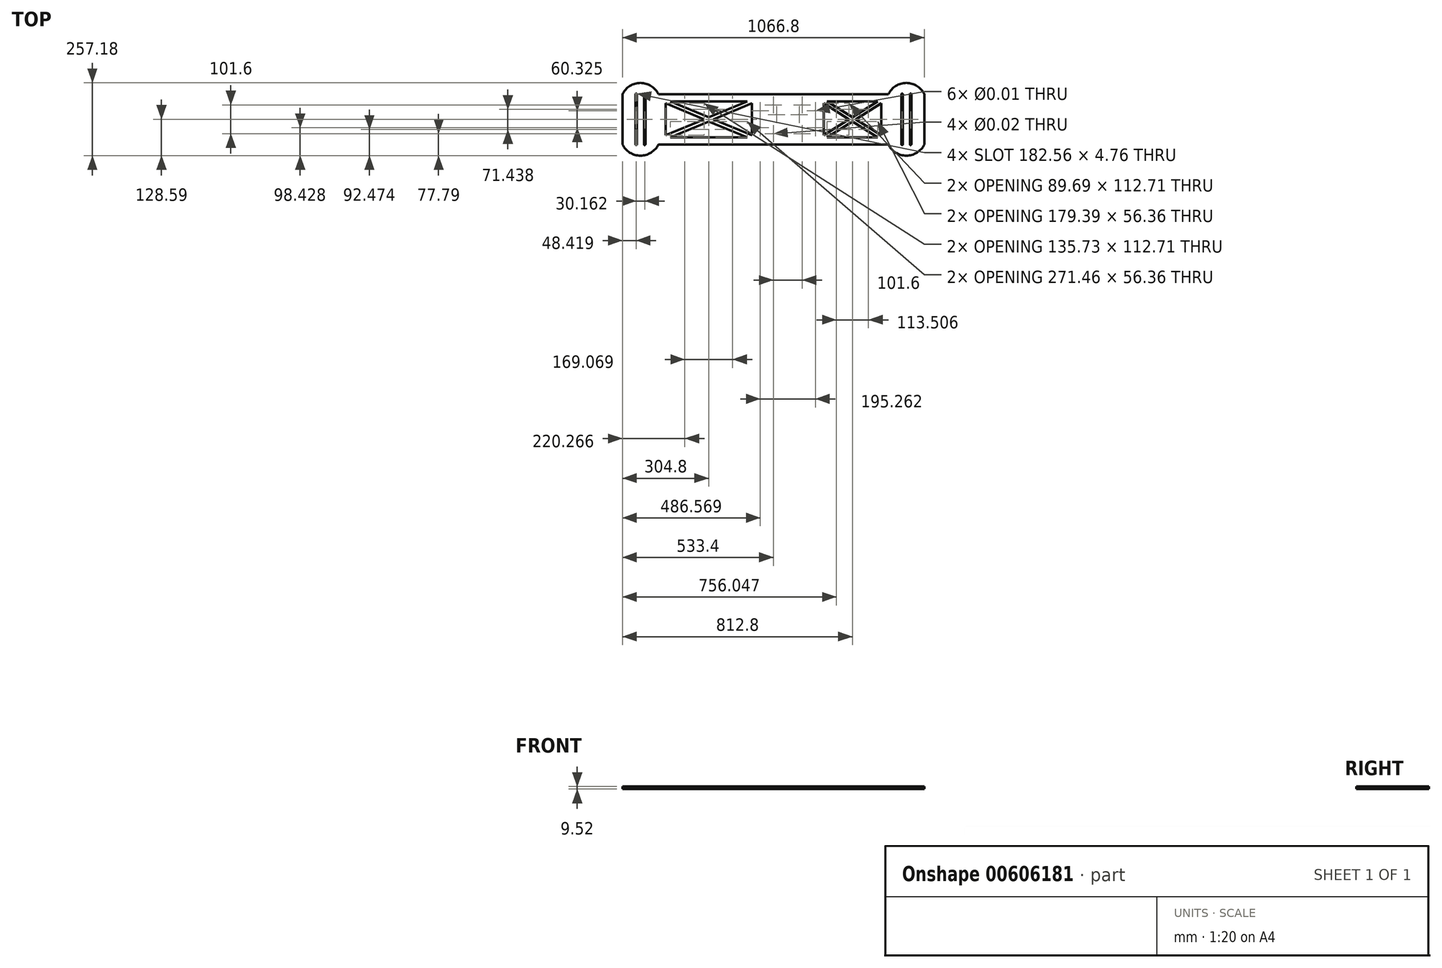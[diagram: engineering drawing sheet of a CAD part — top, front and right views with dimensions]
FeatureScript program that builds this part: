
annotation { "Feature Type Name" : "Feature", "Feature Type Description" : "" }
export const myFeature = defineFeature(function(context is Context, id is Id, definition is map)
    precondition{}
    {
        {
            var Q0;
            Q0=qCreatedBy(makeId("Top.planeOp"),FACE);
            var sketch = newSketch(context, id + "F0", { "sketchPlane" : qUnion([Q0])});
            skLineSegment(sketch, "E0.bottom", {"start": v(406.4, 88.9) * mm, "end": v(-406.4, 88.9) * mm});
            skLineSegment(sketch, "E0.top", {"start": v(406.4, -88.9) * mm, "end": v(-406.4, -88.9) * mm});
            skLineSegment(sketch, "E0.left", {"start": v(533.4, 88.9) * mm, "end": v(533.4, -88.9) * mm});
            skLineSegment(sketch, "E0.right", {"start": v(-533.4, 88.9) * mm, "end": v(-533.4, -88.9) * mm});
            skPoint(sketch, "E0.middle", {"position": v(0, 0) * mm});
            skPoint(sketch, "E1.middle", {"position": v(469.9, 0) * mm});
            skArc(sketch, "E2", {"start": v(406.4, 88.9) * mm, "mid": v(469.9, 128.59) * mm, "end": v(533.4, 88.9) * mm});
            skArc(sketch, "E3.MirrorCS", {"start": v(406.4, -88.9) * mm, "mid": v(469.9, -128.59) * mm, "end": v(533.4, -88.9) * mm});
            skArc(sketch, "E4.MirrorCS", {"start": v(-406.4, 88.9) * mm, "mid": v(-469.9, 128.59) * mm, "end": v(-533.4, 88.9) * mm});
            skArc(sketch, "E5.MirrorCS", {"start": v(-406.4, -88.9) * mm, "mid": v(-469.9, -128.59) * mm, "end": v(-533.4, -88.9) * mm});
            skLineSegment(sketch, "E6", {"start": v(381, 56.36) * mm, "end": v(381, -56.36) * mm});
            skLineSegment(sketch, "E7", {"start": v(381, -56.36) * mm, "end": v(291.3, 0) * mm});
            skLineSegment(sketch, "E8", {"start": v(291.3, 0) * mm, "end": v(381, 56.36) * mm});
            skLineSegment(sketch, "E9", {"start": v(267.5, 0) * mm, "end": v(177.8, 56.36) * mm});
            skLineSegment(sketch, "E10", {"start": v(177.8, 56.36) * mm, "end": v(177.8, -56.36) * mm});
            skLineSegment(sketch, "E11", {"start": v(177.8, -56.36) * mm, "end": v(267.5, 0) * mm});
            skLineSegment(sketch, "E12", {"start": v(279.4, 7.14) * mm, "end": v(189.7, 63.5) * mm});
            skLineSegment(sketch, "E13", {"start": v(189.7, 63.5) * mm, "end": v(369.1, 63.5) * mm});
            skLineSegment(sketch, "E14", {"start": v(369.1, 63.5) * mm, "end": v(279.4, 7.14) * mm});
            skLineSegment(sketch, "E15", {"start": v(279.4, -7.94) * mm, "end": v(189.7, -64.3) * mm});
            skLineSegment(sketch, "E16", {"start": v(189.7, -64.3) * mm, "end": v(369.1, -64.3) * mm});
            skLineSegment(sketch, "E17", {"start": v(369.1, -64.3) * mm, "end": v(279.4, -7.94) * mm});
            skLineSegment(sketch, "E18", {"start": v(-381, 56.36) * mm, "end": v(-381, -56.36) * mm});
            skLineSegment(sketch, "E19", {"start": v(-381, -56.36) * mm, "end": v(-245.27, 0) * mm});
            skLineSegment(sketch, "E20", {"start": v(-245.27, 0) * mm, "end": v(-381, 56.36) * mm});
            skLineSegment(sketch, "E21", {"start": v(-211.93, 0) * mm, "end": v(-76.2, 56.36) * mm});
            skLineSegment(sketch, "E22", {"start": v(-76.2, 56.36) * mm, "end": v(-76.2, -56.36) * mm});
            skLineSegment(sketch, "E23", {"start": v(-76.2, -56.36) * mm, "end": v(-211.93, 0) * mm});
            skLineSegment(sketch, "E24", {"start": v(-228.6, 7.14) * mm, "end": v(-92.87, 63.5) * mm});
            skLineSegment(sketch, "E25", {"start": v(-92.87, 63.5) * mm, "end": v(-364.33, 63.5) * mm});
            skLineSegment(sketch, "E26", {"start": v(-364.33, 63.5) * mm, "end": v(-228.6, 7.14) * mm});
            skLineSegment(sketch, "E27", {"start": v(-228.6, -7.94) * mm, "end": v(-92.87, -64.3) * mm});
            skLineSegment(sketch, "E28", {"start": v(-92.87, -64.3) * mm, "end": v(-364.33, -64.3) * mm});
            skLineSegment(sketch, "E29", {"start": v(-364.33, -64.3) * mm, "end": v(-228.6, -7.94) * mm});
            skLineSegment(sketch, "E30.left", {"start": v(-452.44, 88.9) * mm, "end": v(-452.44, -88.9) * mm});
            skLineSegment(sketch, "E30.right", {"start": v(-457.2, 88.9) * mm, "end": v(-457.2, -88.9) * mm});
            skPoint(sketch, "E30.middle", {"position": v(-454.82, 0) * mm});
            skArc(sketch, "E31", {"start": v(-452.44, -88.9) * mm, "mid": v(-454.82, -91.28) * mm, "end": v(-457.2, -88.9) * mm});
            skArc(sketch, "E32", {"start": v(-452.44, 88.9) * mm, "mid": v(-454.82, 91.28) * mm, "end": v(-457.2, 88.9) * mm});
            skLineSegment(sketch, "E33.left", {"start": v(-482.6, 88.9) * mm, "end": v(-482.6, -88.9) * mm});
            skLineSegment(sketch, "E33.right", {"start": v(-487.36, 88.9) * mm, "end": v(-487.36, -88.9) * mm});
            skPoint(sketch, "E33.middle", {"position": v(-484.98, 0) * mm});
            skArc(sketch, "E34", {"start": v(-482.6, -88.9) * mm, "mid": v(-484.98, -91.28) * mm, "end": v(-487.36, -88.9) * mm});
            skArc(sketch, "E35", {"start": v(-482.6, 88.9) * mm, "mid": v(-484.98, 91.28) * mm, "end": v(-487.36, 88.9) * mm});
            skLineSegment(sketch, "E36.MirrorCS", {"start": v(452.44, 88.9) * mm, "end": v(452.44, -88.9) * mm});
            skArc(sketch, "E37.MirrorCS", {"start": v(452.44, 88.9) * mm, "mid": v(454.82, 91.28) * mm, "end": v(457.2, 88.9) * mm});
            skLineSegment(sketch, "E38.MirrorCS", {"start": v(457.2, 88.9) * mm, "end": v(457.2, -88.9) * mm});
            skArc(sketch, "E39.MirrorCS", {"start": v(452.44, -88.9) * mm, "mid": v(454.82, -91.28) * mm, "end": v(457.2, -88.9) * mm});
            skArc(sketch, "E40.MirrorCS", {"start": v(482.6, -88.9) * mm, "mid": v(484.98, -91.28) * mm, "end": v(487.36, -88.9) * mm});
            skLineSegment(sketch, "E41.MirrorCS", {"start": v(482.6, 88.9) * mm, "end": v(482.6, -88.9) * mm});
            skLineSegment(sketch, "E42", {"start": v(487.36, -88.9) * mm, "end": v(487.36, 88.9) * mm});
            skArc(sketch, "E43", {"start": v(487.36, 88.9) * mm, "mid": v(484.98, 91.28) * mm, "end": v(482.6, 88.9) * mm});
            skSolve(sketch);
        }
        {
            var Q0;
            Q0 = qSketchRegion(id + "F0", true);
            extrude(context, id + "F1", {"entities" : qUnion([Q0]), "endBound" : BoundingType.SYMMETRIC, "depth" : 9.52 * mm, "offsetDistance" : 25.4 * mm});
        }
        {
            var Q0;
            Q0=makeQuery(id+"F1.opExtrude","CAP_FACE",FACE,{"disambiguationData":[OSD([sQuery(id+"F0.wireOp",EDGE,"E0.bottom"),sQuery(id+"F0.wireOp",EDGE,"E0.top"),sQuery(id+"F0.wireOp",EDGE,"E0.left"),sQuery(id+"F0.wireOp",EDGE,"E0.right"),sQuery(id+"F0.wireOp",EDGE,"E2"),sQuery(id+"F0.wireOp",EDGE,"E3.MirrorCS"),sQuery(id+"F0.wireOp",EDGE,"E4.MirrorCS"),sQuery(id+"F0.wireOp",EDGE,"E5.MirrorCS"),sQuery(id+"F0.wireOp",EDGE,"E6"),sQuery(id+"F0.wireOp",EDGE,"E7"),sQuery(id+"F0.wireOp",EDGE,"E8"),sQuery(id+"F0.wireOp",EDGE,"E9"),sQuery(id+"F0.wireOp",EDGE,"E10"),sQuery(id+"F0.wireOp",EDGE,"E11"),sQuery(id+"F0.wireOp",EDGE,"E12"),sQuery(id+"F0.wireOp",EDGE,"E13"),sQuery(id+"F0.wireOp",EDGE,"E14"),sQuery(id+"F0.wireOp",EDGE,"E15"),sQuery(id+"F0.wireOp",EDGE,"E16"),sQuery(id+"F0.wireOp",EDGE,"E17"),sQuery(id+"F0.wireOp",EDGE,"E18"),sQuery(id+"F0.wireOp",EDGE,"E19"),sQuery(id+"F0.wireOp",EDGE,"E20"),sQuery(id+"F0.wireOp",EDGE,"E21"),sQuery(id+"F0.wireOp",EDGE,"E22"),sQuery(id+"F0.wireOp",EDGE,"E23"),sQuery(id+"F0.wireOp",EDGE,"E24"),sQuery(id+"F0.wireOp",EDGE,"E25"),sQuery(id+"F0.wireOp",EDGE,"E26"),sQuery(id+"F0.wireOp",EDGE,"E27"),sQuery(id+"F0.wireOp",EDGE,"E28"),sQuery(id+"F0.wireOp",EDGE,"E29"),sQuery(id+"F0.wireOp",EDGE,"E30.left"),sQuery(id+"F0.wireOp",EDGE,"E30.right"),sQuery(id+"F0.wireOp",EDGE,"E31"),sQuery(id+"F0.wireOp",EDGE,"E32"),sQuery(id+"F0.wireOp",EDGE,"E33.left"),sQuery(id+"F0.wireOp",EDGE,"E33.right"),sQuery(id+"F0.wireOp",EDGE,"E34"),sQuery(id+"F0.wireOp",EDGE,"E35"),sQuery(id+"F0.wireOp",EDGE,"E36.MirrorCS"),sQuery(id+"F0.wireOp",EDGE,"E37.MirrorCS"),sQuery(id+"F0.wireOp",EDGE,"E38.MirrorCS"),sQuery(id+"F0.wireOp",EDGE,"E39.MirrorCS"),sQuery(id+"F0.wireOp",EDGE,"E40.MirrorCS"),sQuery(id+"F0.wireOp",EDGE,"E41.MirrorCS"),sQuery(id+"F0.wireOp",EDGE,"E42"),sQuery(id+"F0.wireOp",EDGE,"E43")])],"isStart":false});
            var sketch = newSketch(context, id + "F2", { "sketchPlane" : qUnion([Q0])});
            skPoint(sketch, "E44", {"position": v(0, 50.8) * mm});
            skPoint(sketch, "E45", {"position": v(101.6, 50.8) * mm});
            skPoint(sketch, "E46", {"position": v(101.6, -50.8) * mm});
            skPoint(sketch, "E47", {"position": v(0, -50.8) * mm});
            skPoint(sketch, "E48", {"position": v(11.11, 16.7) * mm});
            skPoint(sketch, "E49", {"position": v(91.28, 16.7) * mm});
            skPoint(sketch, "E50", {"position": v(148.43, 30.16) * mm});
            skPoint(sketch, "E51", {"position": v(148.43, -30.16) * mm});
            skPoint(sketch, "E52", {"position": v(-46.83, -30.16) * mm});
            skPoint(sketch, "E53", {"position": v(-46.83, 30.16) * mm});
            skSolve(sketch);
        }
        {
            var Q0;
            Q0=sQuery(id+"F2.wireOp",VERTEX,"E44");
            var Q1;
            Q1=sQuery(id+"F2.wireOp",VERTEX,"E45");
            var Q2;
            Q2=sQuery(id+"F2.wireOp",VERTEX,"E46");
            var Q3;
            Q3=sQuery(id+"F2.wireOp",VERTEX,"E47");
            var Q4;
            Q4=makeQuery(id+"F1.opExtrude","SWEPT_BODY",BODY,{"disambiguationData":[OSD([sQuery(id+"F0.wireOp",EDGE,"E0.bottom"),sQuery(id+"F0.wireOp",EDGE,"E0.top"),sQuery(id+"F0.wireOp",EDGE,"E0.left"),sQuery(id+"F0.wireOp",EDGE,"E0.right"),sQuery(id+"F0.wireOp",EDGE,"E2"),sQuery(id+"F0.wireOp",EDGE,"E3.MirrorCS"),sQuery(id+"F0.wireOp",EDGE,"E4.MirrorCS"),sQuery(id+"F0.wireOp",EDGE,"E5.MirrorCS"),sQuery(id+"F0.wireOp",EDGE,"E6"),sQuery(id+"F0.wireOp",EDGE,"E7"),sQuery(id+"F0.wireOp",EDGE,"E8"),sQuery(id+"F0.wireOp",EDGE,"E9"),sQuery(id+"F0.wireOp",EDGE,"E10"),sQuery(id+"F0.wireOp",EDGE,"E11"),sQuery(id+"F0.wireOp",EDGE,"E12"),sQuery(id+"F0.wireOp",EDGE,"E13"),sQuery(id+"F0.wireOp",EDGE,"E14"),sQuery(id+"F0.wireOp",EDGE,"E15"),sQuery(id+"F0.wireOp",EDGE,"E16"),sQuery(id+"F0.wireOp",EDGE,"E17"),sQuery(id+"F0.wireOp",EDGE,"E18"),sQuery(id+"F0.wireOp",EDGE,"E19"),sQuery(id+"F0.wireOp",EDGE,"E20"),sQuery(id+"F0.wireOp",EDGE,"E21"),sQuery(id+"F0.wireOp",EDGE,"E22"),sQuery(id+"F0.wireOp",EDGE,"E23"),sQuery(id+"F0.wireOp",EDGE,"E24"),sQuery(id+"F0.wireOp",EDGE,"E25"),sQuery(id+"F0.wireOp",EDGE,"E26"),sQuery(id+"F0.wireOp",EDGE,"E27"),sQuery(id+"F0.wireOp",EDGE,"E28"),sQuery(id+"F0.wireOp",EDGE,"E29"),sQuery(id+"F0.wireOp",EDGE,"E30.left"),sQuery(id+"F0.wireOp",EDGE,"E30.right"),sQuery(id+"F0.wireOp",EDGE,"E31"),sQuery(id+"F0.wireOp",EDGE,"E32"),sQuery(id+"F0.wireOp",EDGE,"E33.left"),sQuery(id+"F0.wireOp",EDGE,"E33.right"),sQuery(id+"F0.wireOp",EDGE,"E34"),sQuery(id+"F0.wireOp",EDGE,"E35"),sQuery(id+"F0.wireOp",EDGE,"E36.MirrorCS"),sQuery(id+"F0.wireOp",EDGE,"E37.MirrorCS"),sQuery(id+"F0.wireOp",EDGE,"E38.MirrorCS"),sQuery(id+"F0.wireOp",EDGE,"E39.MirrorCS"),sQuery(id+"F0.wireOp",EDGE,"E40.MirrorCS"),sQuery(id+"F0.wireOp",EDGE,"E41.MirrorCS"),sQuery(id+"F0.wireOp",EDGE,"E42"),sQuery(id+"F0.wireOp",EDGE,"E43")])]});
            hole(context, id + "F3", {"style" : HoleStyle.SIMPLE, "endStyle" : HoleEndStyle.THROUGH, "standardTappedOrClearance" : lookupTablePath({ "standard" : "ANSI", "size" : "7/16 (0.44)", "type" : "Drilled" }), "standardBlindInLast" : lookupTablePath({ "standard" : "ANSI", "size" : "7/16", "type" : "Drilled" }), "holeDiameter" : 7 / 406.4 * mm, "majorDiameter" : 12.7 * mm, "isTappedThrough" : true, "tappedDepth" : 47.62 * mm, "tapClearance" : 3, "startFromSketch" : true, "locations" : qUnion([Q0, Q1, Q2, Q3]), "scope" : qUnion([Q4])});
        }
        {
            var Q0;
            Q0=sQuery(id+"F2.wireOp",VERTEX,"E53");
            var Q1;
            Q1=sQuery(id+"F2.wireOp",VERTEX,"E52");
            var Q2;
            Q2=sQuery(id+"F2.wireOp",VERTEX,"E48");
            var Q3;
            Q3=sQuery(id+"F2.wireOp",VERTEX,"E49");
            var Q4;
            Q4=sQuery(id+"F2.wireOp",VERTEX,"E50");
            var Q5;
            Q5=sQuery(id+"F2.wireOp",VERTEX,"E51");
            var Q6;
            Q6=makeQuery(id+"F1.opExtrude","SWEPT_BODY",BODY,{"disambiguationData":[OSD([sQuery(id+"F0.wireOp",EDGE,"E0.bottom"),sQuery(id+"F0.wireOp",EDGE,"E0.top"),sQuery(id+"F0.wireOp",EDGE,"E0.left"),sQuery(id+"F0.wireOp",EDGE,"E0.right"),sQuery(id+"F0.wireOp",EDGE,"E2"),sQuery(id+"F0.wireOp",EDGE,"E3.MirrorCS"),sQuery(id+"F0.wireOp",EDGE,"E4.MirrorCS"),sQuery(id+"F0.wireOp",EDGE,"E5.MirrorCS"),sQuery(id+"F0.wireOp",EDGE,"E6"),sQuery(id+"F0.wireOp",EDGE,"E7"),sQuery(id+"F0.wireOp",EDGE,"E8"),sQuery(id+"F0.wireOp",EDGE,"E9"),sQuery(id+"F0.wireOp",EDGE,"E10"),sQuery(id+"F0.wireOp",EDGE,"E11"),sQuery(id+"F0.wireOp",EDGE,"E12"),sQuery(id+"F0.wireOp",EDGE,"E13"),sQuery(id+"F0.wireOp",EDGE,"E14"),sQuery(id+"F0.wireOp",EDGE,"E15"),sQuery(id+"F0.wireOp",EDGE,"E16"),sQuery(id+"F0.wireOp",EDGE,"E17"),sQuery(id+"F0.wireOp",EDGE,"E18"),sQuery(id+"F0.wireOp",EDGE,"E19"),sQuery(id+"F0.wireOp",EDGE,"E20"),sQuery(id+"F0.wireOp",EDGE,"E21"),sQuery(id+"F0.wireOp",EDGE,"E22"),sQuery(id+"F0.wireOp",EDGE,"E23"),sQuery(id+"F0.wireOp",EDGE,"E24"),sQuery(id+"F0.wireOp",EDGE,"E25"),sQuery(id+"F0.wireOp",EDGE,"E26"),sQuery(id+"F0.wireOp",EDGE,"E27"),sQuery(id+"F0.wireOp",EDGE,"E28"),sQuery(id+"F0.wireOp",EDGE,"E29"),sQuery(id+"F0.wireOp",EDGE,"E30.left"),sQuery(id+"F0.wireOp",EDGE,"E30.right"),sQuery(id+"F0.wireOp",EDGE,"E31"),sQuery(id+"F0.wireOp",EDGE,"E32"),sQuery(id+"F0.wireOp",EDGE,"E33.left"),sQuery(id+"F0.wireOp",EDGE,"E33.right"),sQuery(id+"F0.wireOp",EDGE,"E34"),sQuery(id+"F0.wireOp",EDGE,"E35"),sQuery(id+"F0.wireOp",EDGE,"E36.MirrorCS"),sQuery(id+"F0.wireOp",EDGE,"E37.MirrorCS"),sQuery(id+"F0.wireOp",EDGE,"E38.MirrorCS"),sQuery(id+"F0.wireOp",EDGE,"E39.MirrorCS"),sQuery(id+"F0.wireOp",EDGE,"E40.MirrorCS"),sQuery(id+"F0.wireOp",EDGE,"E41.MirrorCS"),sQuery(id+"F0.wireOp",EDGE,"E42"),sQuery(id+"F0.wireOp",EDGE,"E43")])]});
            hole(context, id + "F4", {"style" : HoleStyle.SIMPLE, "endStyle" : HoleEndStyle.THROUGH, "standardTappedOrClearance" : lookupTablePath({ "standard" : "ANSI", "size" : "5/16 (0.31)", "type" : "Drilled" }), "standardBlindInLast" : lookupTablePath({ "standard" : "ANSI", "size" : "5/16", "type" : "Drilled" }), "holeDiameter" : 5 / 406.4 * mm, "majorDiameter" : 6.35 * mm, "isTappedThrough" : true, "tappedDepth" : 47.62 * mm, "tapClearance" : 3, "startFromSketch" : true, "locations" : qUnion([Q0, Q1, Q2, Q3, Q4, Q5]), "scope" : qUnion([Q6])});
        }
    });
